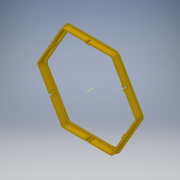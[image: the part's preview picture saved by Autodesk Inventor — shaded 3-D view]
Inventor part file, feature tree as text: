
AUTODESK INVENTOR PART (.ipt)
format: ipt  version: 2019 (Build 230136000, 136)  size: 271,360 bytes
history: native  units: mm
features: extrude x5, sketch x5, projected_geometry x3, fillet x2, other x1, pattern_circular x1
ambient origin geometry x8: Origin, YZ Plane, XZ Plane, XY Plane, X Axis, Y Axis, Z Axis, Center Point
bodies: Solid1 (feature_tree)
feature tree (17):
  extrude  "Extrusion1"  Depth=2.0mm TaperAngle=0.0deg
  extrude  "Extrusion5"  Depth=2.0mm
  extrude  "Extrusion6"  Depth=4.0mm
  fillet  "Fillet1"  Radius=7.0mm
  fillet  "Fillet2"  Radius=10.0mm
  extrude  "Extrusion7"  Depth=10.0mm
  extrude  "Extrusion8"  Depth=6.5mm TaperAngle=0.0deg
  other  "Work Axis2"
  pattern_circular  "Circular Pattern1"  [2 undecoded]
  sketch  "Sketch1"  dims[d0=175.0mm d1=2.0mm d2=0.0mm]
  sketch  "Sketch5"  dims[d15=2.0mm d16=2.0mm]
  projected_geometry  "Projected Loop4"
  sketch  "Sketch7"  dims[d17=10.0mm d18=0.0mm d19=4.0mm d20=7.0mm d21=0.0mm d22=10.0mm]
  projected_geometry  "Projected Loop6"
  sketch  "Sketch8"  dims[d23=4.0mm d24=10.0mm]
  sketch  "Sketch9"  dims[d25=3.0mm d26=6.5mm d27=0.0mm d28=4.0mm d29=3.0mm d30=5.0mm d31=0.0mm d32=60.0mm d33=360.0deg]
  projected_geometry  "Projected Loop7"
note: 2 required parameter values undecoded (feature->parameter linkage not recoverable at this tier; creation-order binding heuristic only, values carry confidence <= 0.55)
